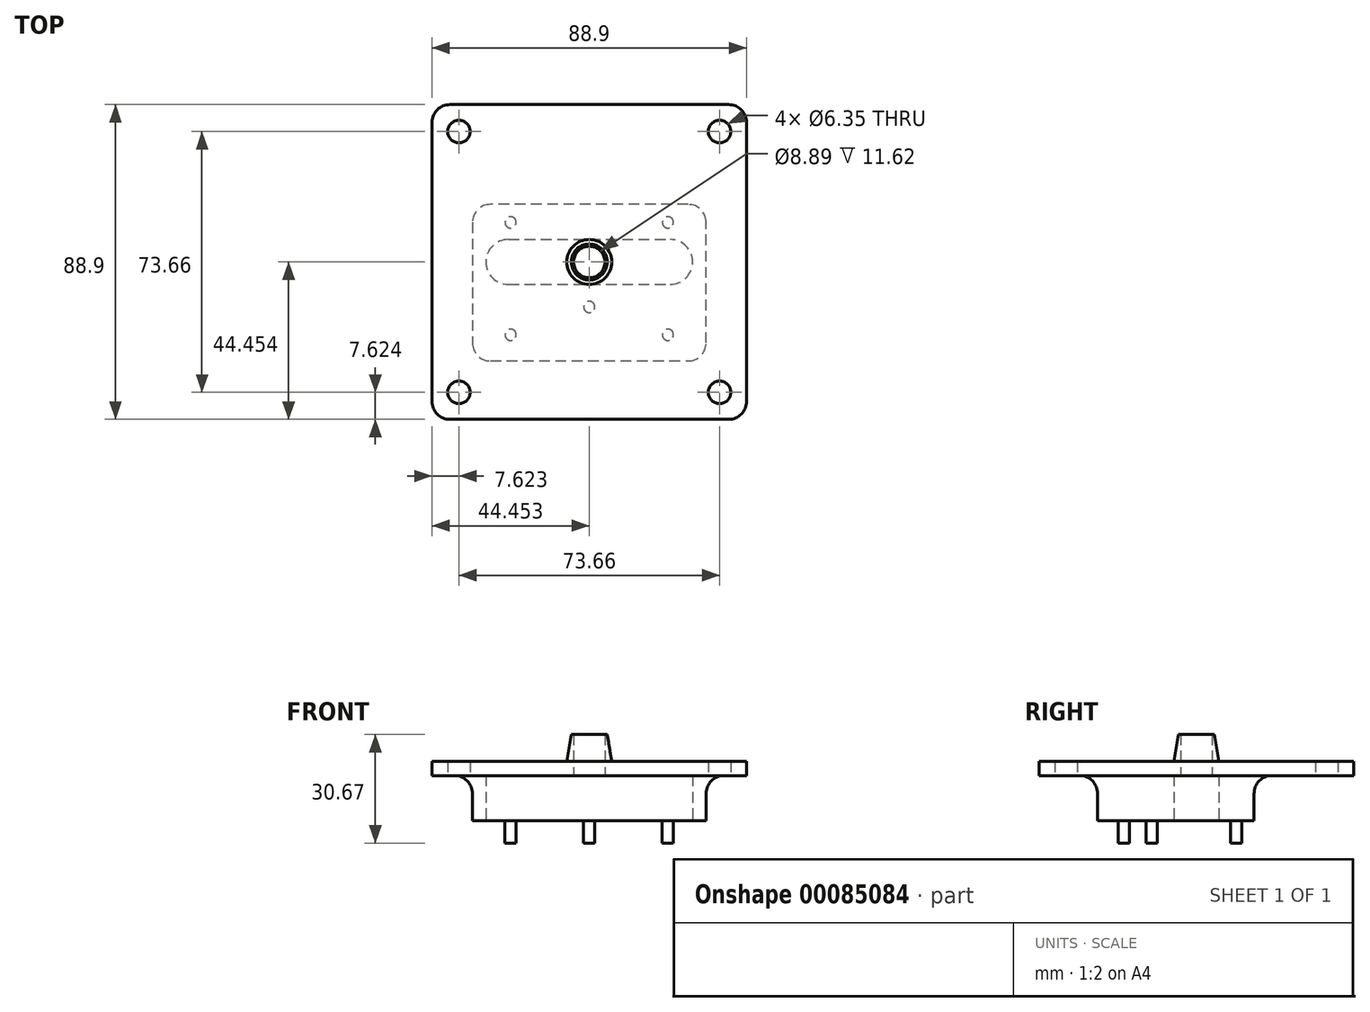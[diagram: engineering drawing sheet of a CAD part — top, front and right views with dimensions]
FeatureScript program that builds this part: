
annotation { "Feature Type Name" : "Feature", "Feature Type Description" : "" }
export const myFeature = defineFeature(function(context is Context, id is Id, definition is map)
    precondition{}
    {
        {
            var Q0;
            Q0=qCreatedBy(makeId("Top.planeOp"),FACE);
            var sketch = newSketch(context, id + "F0", { "sketchPlane" : qUnion([Q0])});
            skLineSegment(sketch, "E0.0.0", {"start": v(7.58, 4.44) * mm, "end": v(-58.46, 4.44) * mm});
            skLineSegment(sketch, "E0.0.1", {"start": v(-58.46, 4.44) * mm, "end": v(-58.46, -39.76) * mm});
            skLineSegment(sketch, "E0.0.2", {"start": v(-58.46, -39.76) * mm, "end": v(7.58, -39.76) * mm});
            skLineSegment(sketch, "E0.0.3", {"start": v(7.58, -39.76) * mm, "end": v(7.58, 4.44) * mm});
            skLineSegment(sketch, "E1.bottom", {"start": v(-48.3, -18.17) * mm, "end": v(-2.58, -18.17) * mm});
            skLineSegment(sketch, "E1.top", {"start": v(-48.3, -5.47) * mm, "end": v(-2.58, -5.47) * mm});
            skLineSegment(sketch, "E1.left", {"start": v(-48.3, -18.17) * mm, "end": v(-48.3, -5.47) * mm});
            skLineSegment(sketch, "E1.right", {"start": v(-2.58, -18.17) * mm, "end": v(-2.58, -5.47) * mm});
            skCircle(sketch, "E2.0", {"center": v(-48.3, -11.82) * mm, "radius": 6.35 * mm});
            skCircle(sketch, "E3.0", {"center": v(-2.58, -11.82) * mm, "radius": 6.35 * mm});
            skSolve(sketch);
        }
        {
            var Q0;
            Q0=makeQuery(id+"F0.imprint","IMPRINT",FACE,{"disambiguationData":[TD([[makeQuery(id+"F0.imprint","IMPRINT",EDGE,{"derivedFrom":sQuery(id+"F0.wireOp",EDGE,"E0.0.0")}),1.0]])]});
            var Q1;
            Q1=sQuery(id+"F0.wireOp",EDGE,"E0.0.0");
            var Q2;
            Q2=sQuery(id+"F0.wireOp",EDGE,"E0.0.1");
            extrude(context, id + "F1", {"entities" : qUnion([Q0]), "surfaceEntities" : qUnion([Q1, Q2]), "depth" : 12.7 * mm});
        }
        {
            var Q0;
            Q0=makeQuery(id+"F1.opExtrude","CAP_FACE",FACE,{"disambiguationData":[OSD([sQuery(id+"F0.wireOp",EDGE,"E0.0.0"),sQuery(id+"F0.wireOp",EDGE,"E0.0.1"),sQuery(id+"F0.wireOp",EDGE,"E0.0.2"),sQuery(id+"F0.wireOp",EDGE,"E0.0.3"),sQuery(id+"F0.wireOp",EDGE,"E1.bottom"),sQuery(id+"F0.wireOp",EDGE,"E1.top"),sQuery(id+"F0.wireOp",EDGE,"E2.0"),sQuery(id+"F0.wireOp",EDGE,"E3.0")])],"isStart":false});
            var sketch = newSketch(context, id + "F2", { "sketchPlane" : qUnion([Q0])});
            skCircle(sketch, "E4", {"center": v(-25.44, -11.82) * mm, "radius": 4.45 * mm});
            skLineSegment(sketch, "E5.bottom", {"start": v(-69.89, 32.63) * mm, "end": v(19.01, 32.63) * mm});
            skLineSegment(sketch, "E5.top", {"start": v(-69.89, -56.27) * mm, "end": v(19.01, -56.27) * mm});
            skLineSegment(sketch, "E5.left", {"start": v(-69.89, 32.63) * mm, "end": v(-69.89, -56.27) * mm});
            skLineSegment(sketch, "E5.right", {"start": v(19.01, 32.63) * mm, "end": v(19.01, -56.27) * mm});
            skCircle(sketch, "E6", {"center": v(-62.27, 25.01) * mm, "radius": 3.18 * mm});
            skCircle(sketch, "E7", {"center": v(11.4, 25.01) * mm, "radius": 3.18 * mm});
            skCircle(sketch, "E8", {"center": v(11.4, -48.65) * mm, "radius": 3.18 * mm});
            skCircle(sketch, "E9", {"center": v(-62.27, -48.65) * mm, "radius": 3.18 * mm});
            skLineSegment(sketch, "E10.0.0", {"start": v(7.58, -39.76) * mm, "end": v(7.58, 4.44) * mm});
            skLineSegment(sketch, "E10.0.1", {"start": v(7.58, 4.44) * mm, "end": v(-58.46, 4.44) * mm});
            skLineSegment(sketch, "E10.0.2", {"start": v(-58.46, 4.44) * mm, "end": v(-58.46, -39.76) * mm});
            skLineSegment(sketch, "E10.0.3", {"start": v(-58.46, -39.76) * mm, "end": v(7.58, -39.76) * mm});
            skArc(sketch, "E11.0", {"start": v(-2.58, -18.17) * mm, "mid": v(3.77, -11.82) * mm, "end": v(-2.58, -5.47) * mm});
            skLineSegment(sketch, "E12.0", {"start": v(-48.3, -18.17) * mm, "end": v(-2.58, -18.17) * mm});
            skArc(sketch, "E13.0", {"start": v(-48.3, -5.47) * mm, "mid": v(-54.65, -11.82) * mm, "end": v(-48.3, -18.17) * mm});
            skLineSegment(sketch, "E14.0", {"start": v(-48.3, -5.47) * mm, "end": v(-2.58, -5.47) * mm});
            skSolve(sketch);
        }
        {
            var Q0;
            Q0 = qSketchRegion(id + "F2", true);
            var Q1;
            Q1=makeQuery(id+"F2.imprint","IMPRINT",FACE,{"disambiguationData":[TD([[makeQuery(id+"F2.imprint","IMPRINT",EDGE,{"derivedFrom":sQuery(id+"F2.wireOp",EDGE,"E4")}),-1.0]])]});
            var Q2;
            Q2=makeQuery(id+"F2.imprint","IMPRINT",FACE,{"disambiguationData":[TD([[makeQuery(id+"F2.imprint","IMPRINT",EDGE,{"derivedFrom":sQuery(id+"F2.wireOp",EDGE,"E10.0.0")}),1.0]])]});
            extrude(context, id + "F3", {"entities" : qUnion([Q0, Q1, Q2]), "operationType" : NewBodyOperationType.ADD, "depth" : 4 * mm});
        }
        {
            var Q0;
            Q0=makeQuery(id+"F3.opExtrude","CAP_FACE",FACE,{"disambiguationData":[OSD([sQuery(id+"F2.wireOp",EDGE,"E4"),sQuery(id+"F2.wireOp",EDGE,"E5.bottom"),sQuery(id+"F2.wireOp",EDGE,"E5.top"),sQuery(id+"F2.wireOp",EDGE,"E5.left"),sQuery(id+"F2.wireOp",EDGE,"E5.right"),sQuery(id+"F2.wireOp",EDGE,"E6"),sQuery(id+"F2.wireOp",EDGE,"E7"),sQuery(id+"F2.wireOp",EDGE,"E8"),sQuery(id+"F2.wireOp",EDGE,"E9")])],"isStart":false});
            var sketch = newSketch(context, id + "F4", { "sketchPlane" : qUnion([Q0])});
            skCircle(sketch, "E15.0", {"center": v(-25.44, -11.82) * mm, "radius": 4.45 * mm});
            skCircle(sketch, "E16", {"center": v(-25.44, -11.82) * mm, "radius": 6.35 * mm});
            skSolve(sketch);
        }
        {
            var Q0;
            Q0 = qSketchRegion(id + "F4", true);
            extrude(context, id + "F5", {"entities" : qUnion([Q0]), "operationType" : NewBodyOperationType.ADD, "depth" : 7.62 * mm});
        }
        {
            var Q0;
            Q0=makeQuery(id+"F5.opExtrude","CAP_EDGE",EDGE,{"disambiguationData":[OSD([sQuery(id+"F4.wireOp",EDGE,"E16")])],"isStart":false});
            chamfer(context, id + "F6", {"entities" : qUnion([Q0]), "chamferType" : ChamferType.TWO_OFFSETS, "width1" : 1.27 * mm, "oppositeDirection" : false, "width2" : 7.62 * mm, "tangentPropagation" : true});
        }
        {
            var Q0;
            Q0=makeQuery(id+"F1.opExtrude","CAP_EDGE",EDGE,{"disambiguationData":[OSD([sQuery(id+"F0.wireOp",EDGE,"E0.0.0")])],"isStart":false});
            var Q1;
            Q1=makeQuery(id+"F1.opExtrude","CAP_EDGE",EDGE,{"disambiguationData":[OSD([sQuery(id+"F0.wireOp",EDGE,"E0.0.1")])],"isStart":false});
            var Q2;
            Q2=makeQuery(id+"F1.opExtrude","CAP_EDGE",EDGE,{"disambiguationData":[OSD([sQuery(id+"F0.wireOp",EDGE,"E0.0.3")])],"isStart":false});
            var Q3;
            Q3=makeQuery(id+"F1.opExtrude","SWEPT_EDGE",EDGE,{"disambiguationData":[OSD([sQuery(id+"F0.wireOp",EDGE,"E0.0.0"),sQuery(id+"F0.wireOp",EDGE,"E0.0.3")])]});
            var Q4;
            Q4=makeQuery(id+"F1.opExtrude","SWEPT_EDGE",EDGE,{"disambiguationData":[OSD([sQuery(id+"F0.wireOp",EDGE,"E0.0.2"),sQuery(id+"F0.wireOp",EDGE,"E0.0.3")])]});
            var Q5;
            Q5=makeQuery(id+"F1.opExtrude","SWEPT_EDGE",EDGE,{"disambiguationData":[OSD([sQuery(id+"F0.wireOp",EDGE,"E0.0.1"),sQuery(id+"F0.wireOp",EDGE,"E0.0.2")])]});
            var Q6;
            Q6=makeQuery(id+"F1.opExtrude","SWEPT_EDGE",EDGE,{"disambiguationData":[OSD([sQuery(id+"F0.wireOp",EDGE,"E0.0.0"),sQuery(id+"F0.wireOp",EDGE,"E0.0.1")])]});
            var Q7;
            Q7=makeQuery(id+"F1.opExtrude","CAP_EDGE",EDGE,{"disambiguationData":[OSD([sQuery(id+"F0.wireOp",EDGE,"E0.0.2")])],"isStart":false});
            var Q8;
            Q8=makeQuery(id+"F1.opExtrude","CAP_EDGE",EDGE,{"disambiguationData":[OSD([sQuery(id+"F0.wireOp",EDGE,"E1.top")])],"isStart":false});
            var Q9;
            Q9=makeQuery(id+"F3.opExtrude","SWEPT_EDGE",EDGE,{"disambiguationData":[OSD([sQuery(id+"F2.wireOp",EDGE,"E5.bottom"),sQuery(id+"F2.wireOp",EDGE,"E5.right")])]});
            var Q10;
            Q10=makeQuery(id+"F3.opExtrude","SWEPT_EDGE",EDGE,{"disambiguationData":[OSD([sQuery(id+"F2.wireOp",EDGE,"E5.bottom"),sQuery(id+"F2.wireOp",EDGE,"E5.left")])]});
            var Q11;
            Q11=makeQuery(id+"F3.opExtrude","SWEPT_EDGE",EDGE,{"disambiguationData":[OSD([sQuery(id+"F2.wireOp",EDGE,"E5.top"),sQuery(id+"F2.wireOp",EDGE,"E5.right")])]});
            var Q12;
            Q12=makeQuery(id+"F3.opExtrude","SWEPT_EDGE",EDGE,{"disambiguationData":[OSD([sQuery(id+"F2.wireOp",EDGE,"E5.top"),sQuery(id+"F2.wireOp",EDGE,"E5.left")])]});
            fillet(context, id + "F7", {"entities" : qUnion([Q0, Q1, Q2, Q3, Q4, Q5, Q6, Q7, Q8, Q9, Q10, Q11, Q12]), "radius" : 5.08 * mm, "tangentPropagation" : true, "allowEdgeOverflow" : false});
        }
        {
            var Q0;
            Q0=makeQuery(id+"F1.opExtrude","CAP_FACE",FACE,{"disambiguationData":[OSD([sQuery(id+"F0.wireOp",EDGE,"E0.0.0"),sQuery(id+"F0.wireOp",EDGE,"E0.0.1"),sQuery(id+"F0.wireOp",EDGE,"E0.0.2"),sQuery(id+"F0.wireOp",EDGE,"E0.0.3"),sQuery(id+"F0.wireOp",EDGE,"E1.bottom"),sQuery(id+"F0.wireOp",EDGE,"E1.top"),sQuery(id+"F0.wireOp",EDGE,"E2.0"),sQuery(id+"F0.wireOp",EDGE,"E3.0")])],"isStart":true});
            var sketch = newSketch(context, id + "F8", { "sketchPlane" : qUnion([Q0])});
            skCircle(sketch, "E17", {"center": v(-47.66, 0.64) * mm, "radius": 1.59 * mm});
            skCircle(sketch, "E18", {"center": v(-3.21, 0.64) * mm, "radius": 1.59 * mm});
            skCircle(sketch, "E19", {"center": v(-47.66, 32.39) * mm, "radius": 1.59 * mm});
            skCircle(sketch, "E20", {"center": v(-25.44, 24.52) * mm, "radius": 1.59 * mm});
            skCircle(sketch, "E21", {"center": v(-3.21, 32.39) * mm, "radius": 1.59 * mm});
            skLineSegment(sketch, "E22.0.0", {"start": v(-53.38, -4.44) * mm, "end": v(2.5, -4.44) * mm});
            skArc(sketch, "E22.0.1", {"start": v(2.5, -4.44) * mm, "mid": v(6.1, -2.96) * mm, "end": v(7.58, 0.64) * mm});
            skLineSegment(sketch, "E22.0.2", {"start": v(7.58, 0.64) * mm, "end": v(7.58, 34.68) * mm});
            skArc(sketch, "E22.0.3", {"start": v(7.58, 34.68) * mm, "mid": v(6.1, 38.27) * mm, "end": v(2.5, 39.76) * mm});
            skLineSegment(sketch, "E22.0.4", {"start": v(2.5, 39.76) * mm, "end": v(-53.38, 39.76) * mm});
            skArc(sketch, "E22.0.5", {"start": v(-53.38, 39.76) * mm, "mid": v(-56.97, 38.27) * mm, "end": v(-58.46, 34.68) * mm});
            skLineSegment(sketch, "E22.0.6", {"start": v(-58.46, 34.68) * mm, "end": v(-58.46, 0.64) * mm});
            skArc(sketch, "E22.0.7", {"start": v(-58.46, 0.64) * mm, "mid": v(-56.97, -2.96) * mm, "end": v(-53.38, -4.44) * mm});
            skSolve(sketch);
        }
        {
            var Q0;
            Q0=makeQuery(id+"F8.imprint","IMPRINT",FACE,{"disambiguationData":[TD([[makeQuery(id+"F8.imprint","IMPRINT",EDGE,{"derivedFrom":sQuery(id+"F8.wireOp",EDGE,"E19")}),1.0]])]});
            var Q1;
            Q1=makeQuery(id+"F8.imprint","IMPRINT",FACE,{"disambiguationData":[TD([[makeQuery(id+"F8.imprint","IMPRINT",EDGE,{"derivedFrom":sQuery(id+"F8.wireOp",EDGE,"E20")}),1.0]])]});
            var Q2;
            Q2=makeQuery(id+"F8.imprint","IMPRINT",FACE,{"disambiguationData":[TD([[makeQuery(id+"F8.imprint","IMPRINT",EDGE,{"derivedFrom":sQuery(id+"F8.wireOp",EDGE,"E21")}),1.0]])]});
            var Q3;
            Q3=makeQuery(id+"F8.imprint","IMPRINT",FACE,{"disambiguationData":[TD([[makeQuery(id+"F8.imprint","IMPRINT",EDGE,{"derivedFrom":sQuery(id+"F8.wireOp",EDGE,"E18")}),1.0]])]});
            var Q4;
            Q4=makeQuery(id+"F8.imprint","IMPRINT",FACE,{"disambiguationData":[TD([[makeQuery(id+"F8.imprint","IMPRINT",EDGE,{"derivedFrom":sQuery(id+"F8.wireOp",EDGE,"E17")}),1.0]])]});
            extrude(context, id + "F9", {"entities" : qUnion([Q0, Q1, Q2, Q3, Q4]), "operationType" : NewBodyOperationType.ADD, "depth" : 6.35 * mm});
        }
    });
